# Revit family: 34_LB_UNIQ_SB-O1S
name_source: partatom
category: Generic Models
revit_build: Autodesk Revit 2016 (Build: 20150714_1515(x64)
units: mm (PartAtom-declared; Revit-internal decimal feet)

## family parameters
Can host rebar = No
Cut with Voids When Loaded = No
Part Type = Normal
Room Calculation Point = No
Round Connector Dimension = Use Diameter
Shared = No
Work Plane-Based = No

## types (1)
- UNIQ_SB-O1S
    Assembly Code = 34.11
    Bovenrailing = Yes
    Cover_front_CF-300 = Yes
    Cover_front_CF-303 = No
    Cover_front_CF-312 = No
    Cover_front_CF-320 = No
    Description = UNIQ SB-O1S | VLOERMONTAGE
    Dikte_glas = 22 mm
    Gasdiktes = Geschikt voor 8/8 pvb, 10/10 pvb en 15
    Glas_dikte = 22 mm
    IfcExportAs = IfcRailing
    Krachten = Geschikt voor maximaal 1 KN
    Manufacturer = SB Railing
    Materiaal_afdekker = Aluminium
    Materiaal_glas = Glass
    Materiaal_pakking = Pakking
    Materiaal_profiel = Aluminium
    Materiaal_ribber = Rubber
    Model = UNIQ_SB-O1S
    URL = https://uniq-balustrades.com
    Uitvoering = RVS look (standaard) materiaal is geanodiseerd en geschik voor binnen en buitengebruik.
    Verstelbaar profiel = nee

## geometry (parser evidence)
native form markers: Sweep x20
no freeform markers — native parametric forms only
